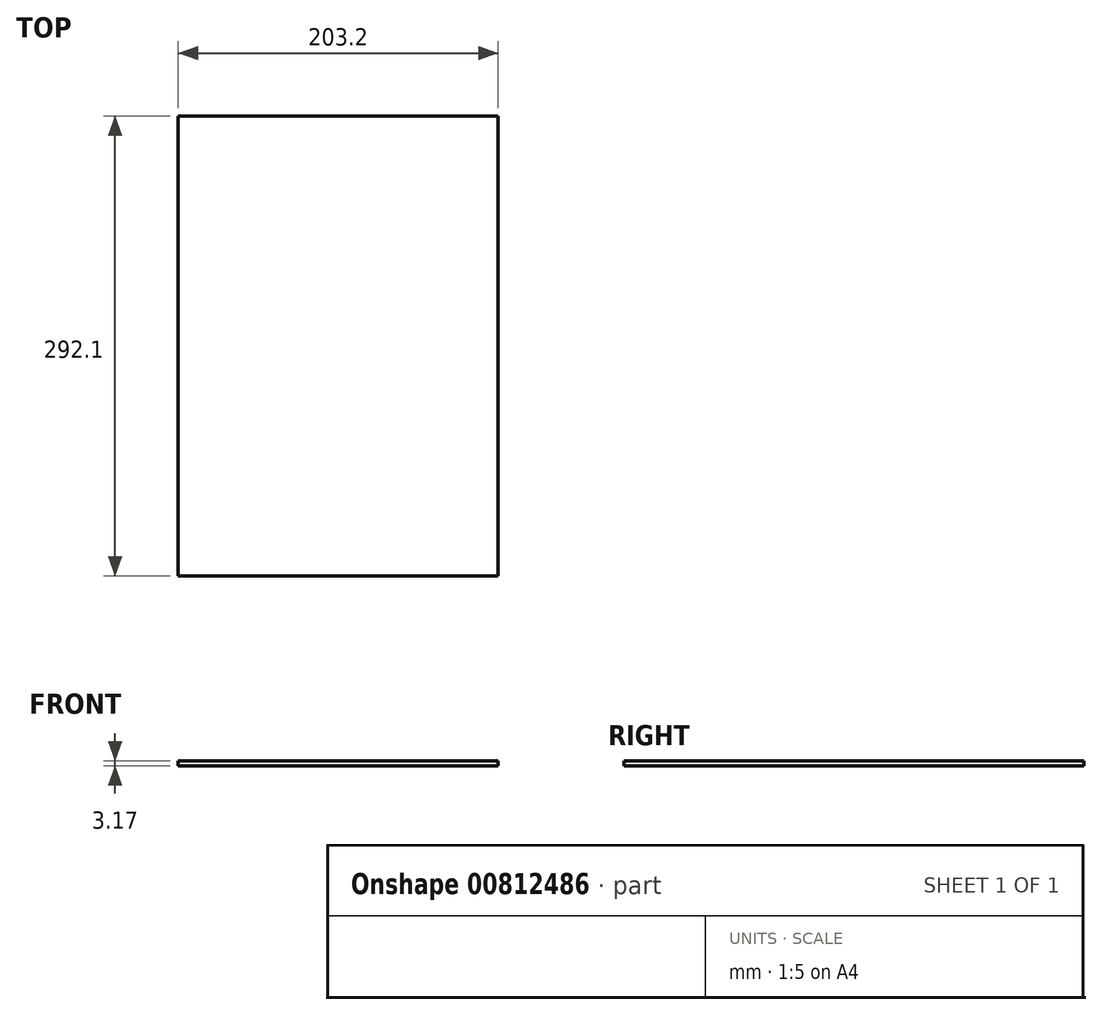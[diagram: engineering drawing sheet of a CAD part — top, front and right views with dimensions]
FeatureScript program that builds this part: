
annotation { "Feature Type Name" : "Feature", "Feature Type Description" : "" }
export const myFeature = defineFeature(function(context is Context, id is Id, definition is map)
    precondition{}
    {
        {
            var Q0;
            Q0=qCreatedBy(makeId("Top.planeOp"),FACE);
            var sketch = newSketch(context, id + "F0", { "sketchPlane" : qUnion([Q0])});
            skLineSegment(sketch, "E0.bottom", {"start": v(0, 0) * mm, "end": v(203.2, 0) * mm});
            skLineSegment(sketch, "E0.top", {"start": v(0, 292.1) * mm, "end": v(203.2, 292.1) * mm});
            skLineSegment(sketch, "E0.left", {"start": v(0, 0) * mm, "end": v(0, 292.1) * mm});
            skLineSegment(sketch, "E0.right", {"start": v(203.2, 0) * mm, "end": v(203.2, 292.1) * mm});
            skSolve(sketch);
        }
        {
            var Q0;
            Q0 = qSketchRegion(id + "F0", true);
            extrude(context, id + "F1", {"entities" : qUnion([Q0]), "depth" : 3.17 * mm, "offsetDistance" : 25.4 * mm});
        }
    });
